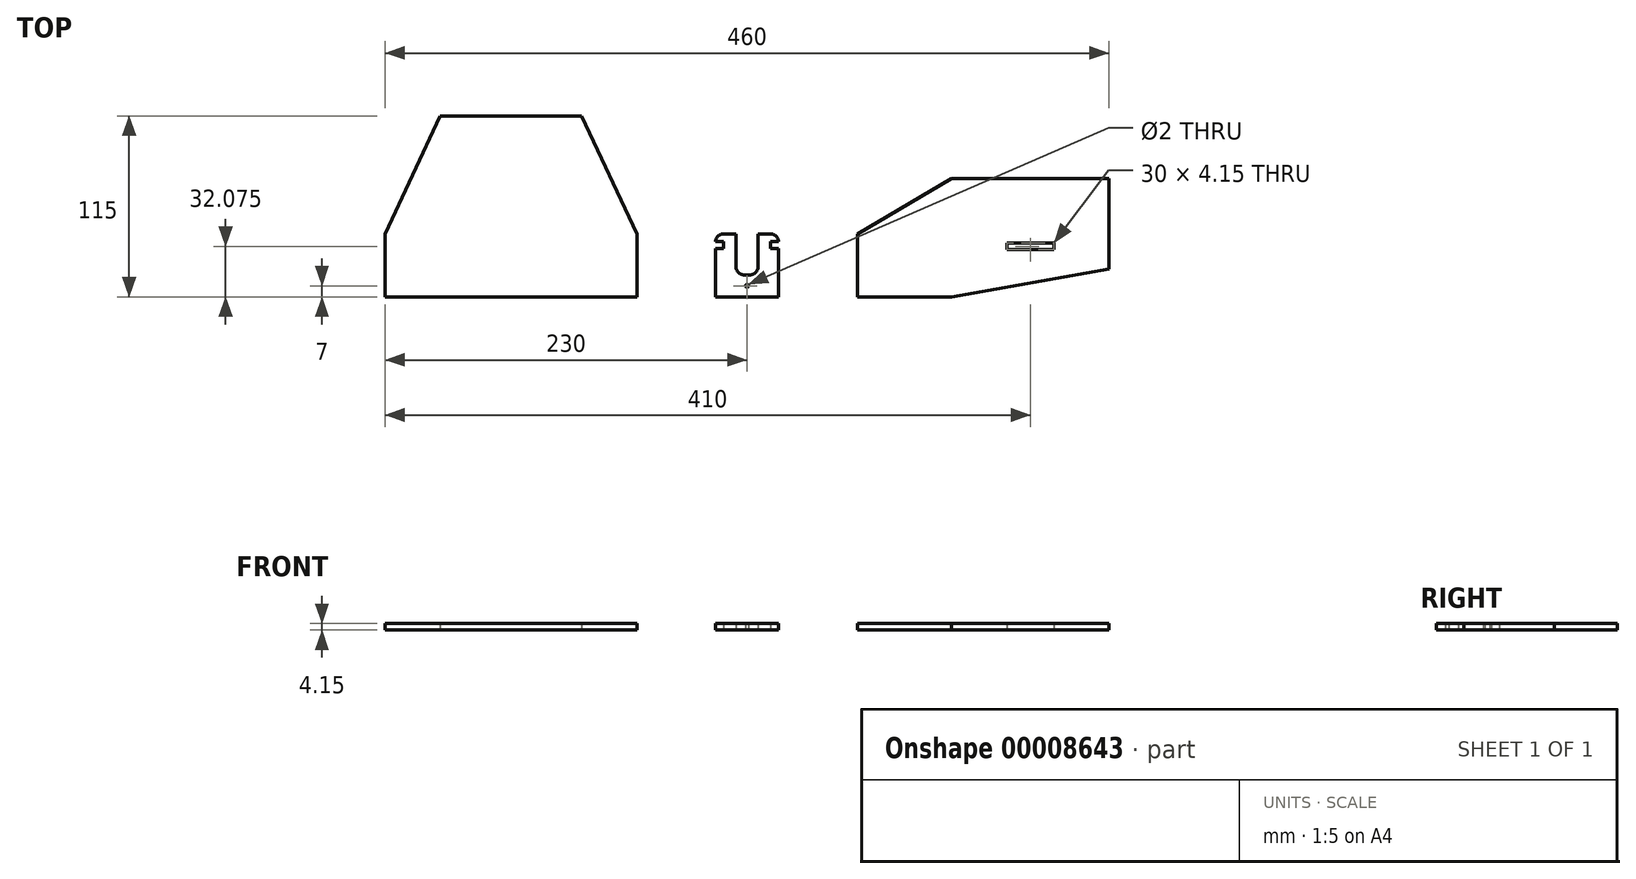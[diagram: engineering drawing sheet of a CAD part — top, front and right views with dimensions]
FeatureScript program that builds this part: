
annotation { "Feature Type Name" : "Feature", "Feature Type Description" : "" }
export const myFeature = defineFeature(function(context is Context, id is Id, definition is map)
    precondition{}
    {
        {
            var Q0;
            Q0=qCreatedBy(makeId("Top.planeOp"),FACE);
            var sketch = newSketch(context, id + "F0", { "sketchPlane" : qUnion([Q0])});
            skLineSegment(sketch, "E0", {"start": v(0, 0) * mm, "end": v(0, 40) * mm});
            skLineSegment(sketch, "E1", {"start": v(60, 75) * mm, "end": v(60, 0) * mm});
            skLineSegment(sketch, "E2", {"start": v(60, 0) * mm, "end": v(0, 0) * mm});
            skLineSegment(sketch, "E3", {"start": v(60, 75) * mm, "end": v(160, 75) * mm});
            skLineSegment(sketch, "E4", {"start": v(160, 75) * mm, "end": v(160, 17.63) * mm});
            skLineSegment(sketch, "E5", {"start": v(160, 17.63) * mm, "end": v(60, 0) * mm});
            skLineSegment(sketch, "E6", {"start": v(-90, 35) * mm, "end": v(-90, 35) * mm});
            skLineSegment(sketch, "E7", {"start": v(-90, 0) * mm, "end": v(-50, 0) * mm});
            skLineSegment(sketch, "E8", {"start": v(-50, 0) * mm, "end": v(-50, 30.85) * mm});
            skLineSegment(sketch, "E9", {"start": v(-55, 40) * mm, "end": v(-63, 40) * mm});
            skLineSegment(sketch, "E10", {"start": v(-63, 40) * mm, "end": v(-63, 19) * mm});
            skLineSegment(sketch, "E11", {"start": v(-68, 14) * mm, "end": v(-72, 14) * mm});
            skLineSegment(sketch, "E12", {"start": v(-77, 19) * mm, "end": v(-77, 40) * mm});
            skLineSegment(sketch, "E13", {"start": v(-77, 40) * mm, "end": v(-85, 40) * mm});
            skLineSegment(sketch, "E14.trimOffspring", {"start": v(-90, 30.85) * mm, "end": v(-90, 0) * mm});
            skLineSegment(sketch, "E15.trimOffspring", {"start": v(-50, 35) * mm, "end": v(-50, 35) * mm});
            skLineSegment(sketch, "E16", {"start": v(-56.5, 40) * mm, "end": v(-56.5, 0) * mm, "construction": true});
            skLineSegment(sketch, "E17", {"start": v(95, 34.15) * mm, "end": v(95, 30) * mm});
            skLineSegment(sketch, "E18", {"start": v(95, 30) * mm, "end": v(125, 30) * mm});
            skLineSegment(sketch, "E19", {"start": v(125, 30) * mm, "end": v(125, 34.15) * mm});
            skLineSegment(sketch, "E20", {"start": v(125, 34.15) * mm, "end": v(95, 34.15) * mm});
            skPoint(sketch, "E21", {"position": v(110, 34.15) * mm});
            skLineSegment(sketch, "E22", {"start": v(110, 34.15) * mm, "end": v(110, 75) * mm, "construction": true});
            skLineSegment(sketch, "E23", {"start": v(-90, 35) * mm, "end": v(-85, 35) * mm});
            skLineSegment(sketch, "E24", {"start": v(-85, 35) * mm, "end": v(-85, 30.85) * mm});
            skLineSegment(sketch, "E25", {"start": v(-85, 30.85) * mm, "end": v(-90, 30.85) * mm});
            skLineSegment(sketch, "E26", {"start": v(-50, 30.85) * mm, "end": v(-55, 30.85) * mm});
            skLineSegment(sketch, "E27", {"start": v(-55, 30.85) * mm, "end": v(-55, 35) * mm});
            skLineSegment(sketch, "E28", {"start": v(-55, 35) * mm, "end": v(-50, 35) * mm});
            skLineSegment(sketch, "E29", {"start": v(-85, 35) * mm, "end": v(-85, 40) * mm, "construction": true});
            skPoint(sketch, "E30.visualSharp", {"position": v(-90, 40) * mm});
            skArc(sketch, "E30.filletArc", {"start": v(-85, 40) * mm, "mid": v(-88.54, 38.54) * mm, "end": v(-90, 35) * mm});
            skPoint(sketch, "E31.visualSharp", {"position": v(-50, 40) * mm});
            skArc(sketch, "E31.filletArc", {"start": v(-50, 35) * mm, "mid": v(-51.46, 38.54) * mm, "end": v(-55, 40) * mm});
            skPoint(sketch, "E32.visualSharp", {"position": v(-77, 14) * mm});
            skArc(sketch, "E32.filletArc", {"start": v(-77, 19) * mm, "mid": v(-75.54, 15.46) * mm, "end": v(-72, 14) * mm});
            skPoint(sketch, "E33.visualSharp", {"position": v(-63, 14) * mm});
            skArc(sketch, "E33.filletArc", {"start": v(-68, 14) * mm, "mid": v(-64.46, 15.46) * mm, "end": v(-63, 19) * mm});
            skPoint(sketch, "E34", {"position": v(-70, 0) * mm});
            skCircle(sketch, "E35", {"center": v(-70, 7) * mm, "radius": 1 * mm});
            skLineSegment(sketch, "E36", {"start": v(-70, 7) * mm, "end": v(-70, 14) * mm, "construction": true});
            skLineSegment(sketch, "E37", {"start": v(-70, 7) * mm, "end": v(-70, 0) * mm, "construction": true});
            skLineSegment(sketch, "E38", {"start": v(60, 0) * mm, "end": v(110, 0) * mm, "construction": true});
            skLineSegment(sketch, "E39", {"start": v(110, 30) * mm, "end": v(110, 0) * mm, "construction": true});
            skLineSegment(sketch, "E40", {"start": v(-50, 0) * mm, "end": v(0, 0) * mm, "construction": true});
            skLineSegment(sketch, "E41", {"start": v(60, 75) * mm, "end": v(0, 40) * mm});
            skLineSegment(sketch, "E42", {"start": v(-240, 40) * mm, "end": v(-240, 0) * mm});
            skLineSegment(sketch, "E43", {"start": v(-200, 40) * mm, "end": v(-200, 0) * mm});
            skLineSegment(sketch, "E44", {"start": v(-300, 0) * mm, "end": v(-140, 0) * mm});
            skLineSegment(sketch, "E45", {"start": v(-140, 0) * mm, "end": v(-140, 40) * mm});
            skLineSegment(sketch, "E46", {"start": v(-300, 40) * mm, "end": v(-300, 0) * mm});
            skLineSegment(sketch, "E47", {"start": v(-300, 40) * mm, "end": v(-240, 40) * mm});
            skLineSegment(sketch, "E48", {"start": v(-200, 40) * mm, "end": v(-140, 40) * mm});
            skLineSegment(sketch, "E49", {"start": v(-200, 40) * mm, "end": v(-240, 40) * mm});
            skLineSegment(sketch, "E50", {"start": v(-240, 115) * mm, "end": v(-200, 115) * mm});
            skLineSegment(sketch, "E51", {"start": v(-200, 115) * mm, "end": v(-200, 40) * mm});
            skLineSegment(sketch, "E52", {"start": v(-240, 40) * mm, "end": v(-240, 115) * mm});
            skLineSegment(sketch, "E53", {"start": v(-140, 0) * mm, "end": v(-90, 0) * mm, "construction": true});
            skLineSegment(sketch, "E54", {"start": v(-200, 115) * mm, "end": v(-175, 115) * mm});
            skLineSegment(sketch, "E55", {"start": v(-175, 115) * mm, "end": v(-140, 40) * mm});
            skLineSegment(sketch, "E56", {"start": v(-240, 115) * mm, "end": v(-265, 115) * mm});
            skLineSegment(sketch, "E57", {"start": v(-265, 115) * mm, "end": v(-300, 40) * mm});
            skLineSegment(sketch, "E58", {"start": v(-77, 40) * mm, "end": v(-63, 40) * mm});
            skSolve(sketch);
        }
        {
            var Q0;
            {var subQ2=sQuery(id+"F0.wireOp",EDGE,"E42");Q0=makeQuery(id+"F0.imprint","IMPRINT",FACE,{"disambiguationData":[TD([[makeQuery(id+"F0.imprint","IMPRINT",EDGE,{"derivedFrom":subQ2}),-1.0]])]});}
            var Q1;
            Q1=makeQuery(id+"F0.imprint","IMPRINT",FACE,{"disambiguationData":[TD([[makeQuery(id+"F0.imprint","IMPRINT",EDGE,{"derivedFrom":sQuery(id+"F0.wireOp",EDGE,"E0")}),-1.0]])]});
            var Q2;
            Q2=makeQuery(id+"F0.imprint","IMPRINT",FACE,{"disambiguationData":[TD([[makeQuery(id+"F0.imprint","IMPRINT",EDGE,{"derivedFrom":sQuery(id+"F0.wireOp",EDGE,"E1")}),1.0]])]});
            var Q3;
            Q3=makeQuery(id+"F0.imprint","IMPRINT",FACE,{"disambiguationData":[TD([[makeQuery(id+"F0.imprint","IMPRINT",EDGE,{"derivedFrom":sQuery(id+"F0.wireOp",EDGE,"E49")}),-1.0]])]});
            var Q4;
            {var subQ2=sQuery(id+"F0.wireOp",EDGE,"E42");Q4=makeQuery(id+"F0.imprint","IMPRINT",FACE,{"disambiguationData":[TD([[makeQuery(id+"F0.imprint","IMPRINT",EDGE,{"derivedFrom":subQ2}),1.0]])]});}
            var Q5;
            Q5=makeQuery(id+"F0.imprint","IMPRINT",FACE,{"disambiguationData":[TD([[makeQuery(id+"F0.imprint","IMPRINT",EDGE,{"derivedFrom":sQuery(id+"F0.wireOp",EDGE,"E47")}),1.0]])]});
            var Q6;
            Q6=makeQuery(id+"F0.imprint","IMPRINT",FACE,{"disambiguationData":[TD([[makeQuery(id+"F0.imprint","IMPRINT",EDGE,{"derivedFrom":sQuery(id+"F0.wireOp",EDGE,"E48")}),1.0]])]});
            var Q7;
            {var subQ2=sQuery(id+"F0.wireOp",EDGE,"E43");Q7=makeQuery(id+"F0.imprint","IMPRINT",FACE,{"disambiguationData":[TD([[makeQuery(id+"F0.imprint","IMPRINT",EDGE,{"derivedFrom":subQ2}),1.0]])]});}
            var Q8;
            Q8=makeQuery(id+"F0.imprint","IMPRINT",FACE,{"disambiguationData":[TD([[makeQuery(id+"F0.imprint","IMPRINT",EDGE,{"derivedFrom":sQuery(id+"F0.wireOp",EDGE,"E7")}),1.0]])]});
            extrude(context, id + "F1", {"entities" : qUnion([Q0, Q1, Q2, Q3, Q4, Q5, Q6, Q7, Q8]), "depth" : 4.15 * mm});
        }
    });
